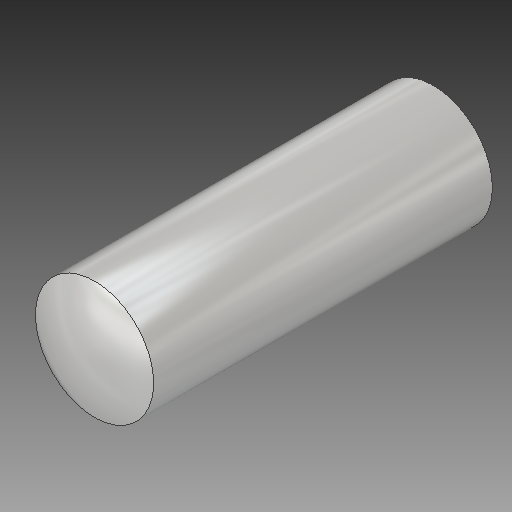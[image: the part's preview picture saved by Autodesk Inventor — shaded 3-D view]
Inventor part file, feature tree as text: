
AUTODESK INVENTOR PART (.ipt)
format: ipt  version: 2018 (Build 220112000, 112)  size: 135,680 bytes
history: native  units: in
note: dims shown in document units (in); Inventor stores cm internally (conversion verified against a paired STEP export)
features: sketch x2, extrude x1, revolve x1
ambient origin geometry x8: Origin, YZ Plane, XZ Plane, XY Plane, X Axis, Y Axis, Z Axis, Center Point
bodies: Solid1 (feature_tree)
feature tree (4):
  extrude  "Extrusion1"  Depth=0.1181in TaperAngle=0.0deg
  revolve  "Revolution1"  [1 undecoded]
  sketch  "Sketch1"  dims[d0=0.1181in d1=0.3543in d2=0.0in]
  sketch  "Sketch2"  dims[d3=0.2362in d4=0.1181in d5=180.0deg]
note: 1 required parameter value undecoded (feature->parameter linkage not recoverable at this tier; creation-order binding heuristic only, values carry confidence <= 0.55)
